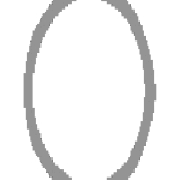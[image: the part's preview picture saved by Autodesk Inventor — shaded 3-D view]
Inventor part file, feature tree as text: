
AUTODESK INVENTOR PART (.ipt)
format: ipt  version: 2021 (Build 250183000, 183)  size: 111,616 bytes
history: native  units: in
note: dims shown in document units (in); Inventor stores cm internally (conversion verified against a paired STEP export)
features: other x4, sketch x3, plane x1
ambient origin geometry x8: Origin, YZ Plane, XZ Plane, XY Plane, X Axis, Y Axis, Z Axis, Center Point
bodies: Solid1 (feature_tree), Body (feature_tree)
feature tree (8):
  other  "Driven Length"
  other  "Frame Generator"
  other  "Start Plane"
  other  "End Plane"
  sketch  "Sketch"  dims[d2=32.7942in d4=-0.0in d5=32.7942in d6=0.12in d7=0.0in d8=90.0deg d9=32.7942in]
  sketch  "Sketch2"  dims[d0=1.0in]
  plane  "Work Plane3"
  sketch  "Sketch3"  dims[d1=0.065in]
